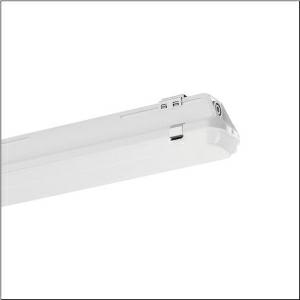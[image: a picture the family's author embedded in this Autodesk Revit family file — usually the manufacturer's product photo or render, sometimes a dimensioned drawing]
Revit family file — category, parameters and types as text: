
# Revit family: monsun_r__11_51fp11mp4b0u_7fbb
name_source: partatom
category: Lighting Fixtures
units: mm (PartAtom-declared; Revit-internal decimal feet)

## family parameters
Cut with Voids When Loaded = No
Host = Face
Light Source = No
Part Type = Normal
Room Calculation Point = No
Round Connector Dimension = Use Diameter
Shared = No

## types (1)
- --- (1 x LED, 11900 lm, 62.4 W, 4000K)
    Apparent Load = 62 VA
    CIE Flux Codes = 71 88 97 97 100
    Color Rendering = 80
    Color Temperature = 4000K
    Default Elevation = 1800 mm
    Description = Monsun® 11, damp-proof luminaire, chain hanger, primary optical cover: enclosure, of PMMA, light emission: direct distribution, primary light characteristic: symmetric, installation type: suspended mounting, surface-mounted, horizontal mounting, vertical mounting, LED, rated luminous flux: 11.900lm, luminous efficacy: 191lm/W, light colour: 840, colour temperature: 4000K, control gear: ON/OFF Multilumen, with terminal, 3-pole, max. 2.5mm², mains connection: 220..240V, AC, 50/60Hz, rated input power: 62W, luminaire housing, of glass-fibre reinforced polyester, uncoated, bright grey, incl. chain hanger, length: 1.590mm, width: 90mm, height: 88mm, clip for enclosure, of stainless steel (V2A), ceiling mounting element, of stainless steel (V2A), chain hanger, of stainless steel (V2A), protection rating (complete): IP66, insulation class (complete): insulation class I (protective earthing), certification: CE, ENEC, VDE, UKCA, protection symbol: D, impact resistance: IK04, permissible operating ambient temperature: -35..+35°C, standard: EN 50419, EN 60598-2-1, contact your sales advisor before using the luminaires in applications with unclear chemical exposure, large temperature fluctuations or condensation-forming humidity, LABS conformity tested according to VDMA 24364:2018-05, no direct snow, no direct sun, no direct rain, for indoor or canopied outdoor use, corresponds to IFS (International Featured Standards) requirements for safety and quality in the food industry, packaging unit: 1 piece
    Height = 89 mm
    Lamp = 1 x LED
    Lamp Light Flux = 11900 lm
    Lamp Power = 62.4 W
    Lamp count = 1
    Length = 1590 mm
    Luminous efficacy = 191 lm/W
    Manufacturer = Siteco
    ModVariant = No
    Model = 51FP11MP4B0U
    Mounting Place = Ceiling
    Mounting Type = Surface mounted
    Number of Poles = 1
    OnlyDefault = Yes
    Power Factor = 1
    Product Name = Monsun® 11
    Product group = damp-proof luminaire
    ProductGroupID = 301
    Protection Class = Protection class I
    Protection Degree = IP 66
    RLX_Detail_Level = 1
    RLX_Emergency_Light_Flux = 0 lm
    RLX_Emergency_Type = 0
    RLX_Emergency_Type_DB = No
    RlxData = <blob elided: 89861 chars, md5=06875060>
    Socket = socket
    Standby Power = 0 W
    System Light Flux = 11900 lm
    System Power = 62 W
    Type Comments = factory setting: luminous flux: 100 % | (A | C | E) | 147 mA
    Type Image = l_1349237.jpg
    URL = http://relux.com
    VarID = @adj_038643
    Voltage = 0 V
    Weight = 0.00 kg
    Width = 90 mm

## geometry (parser evidence)
native form markers: Blend x4, Sweep x10
no freeform markers — native parametric forms only
